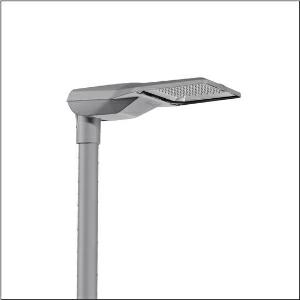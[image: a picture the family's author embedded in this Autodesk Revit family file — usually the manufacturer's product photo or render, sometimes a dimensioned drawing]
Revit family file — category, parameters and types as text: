
# Revit family: streetlight_sl_21_midi___st1_0a_5xe7d63a08nb_cbba
name_source: partatom
category: Lighting Fixtures
units: mm (PartAtom-declared; Revit-internal decimal feet)

## family parameters
Cut with Voids When Loaded = No
Host = Face
Light Source = No
Part Type = Normal
Room Calculation Point = No
Round Connector Dimension = Use Diameter
Shared = No

## types (1)
- --- (1 x LED, 20350 lm, 151.2 W, 2700K)
    Apparent Load = 151 VA
    CIE Flux Codes = 40 73 97 100 100
    Color Rendering = 70
    Color Temperature = 2700K
    Default Elevation = 1800 mm
    Description = Streetlight SL 21 midi, mast luminaire, primary light control with lens, of PMMA, primary optical cover: cover, of toughened safety glass, transparent, light distribution: ST1.0a, light emission: direct distribution, primary light characteristic: asymmetric, installation type: post-top, side-entry, LED, 3G 1.5mm², High Power LED, rated luminous flux: 20.350lm, luminous efficacy: 135lm/W, light colour: 727, colour temperature: 2700K, control: overheat protection, constant luminous flux control, time-dependent luminous flux control, flexible luminous flux parameterisation, mains connection: 220..240V, AC, 50/60Hz, connection cable pre-assembled, cable length: 12,5m, wiring characteristics: H07RN-F, start of lifetime: 151W, end of service life: 157W, reduction: 70W, luminaire housing, of diecast aluminium, powder-coated, Siteco® metallic grey (DB 702S), corrosivity category C5 mid according to DIN EN ISO 12944, please order mast flange separately, inclination adjustable: 0°, 5°, 10°, 15°, sealing non-destructively replaceable, multi-level sealing system, length: 644mm, width: 335mm, height: 110mm, mast flange for spigot size: 42mm (side-entry): 5XC10008XM4, 60/48mm (side-entry/post-top): 5XC10108XM2, 76/60mm (side-entry/post-top): 5XC10108XM1, protection rating (complete): IP66, insulation class (complete): insulation class II (safety insulation), certification: CE, ENEC, ENEC+, VDE, impact resistance: IK09, permissible operating ambient temperature for outdoor applications: -40..+50°C, standard-compliant lighting for roads and squares, packaging unit: 1 piece

Light Distribution: ST1.0a
    Height = 111 mm
    Lamp = 1 x LED
    Lamp Light Flux = 20350 lm
    Lamp Power = 151.2 W
    Lamp count = 1
    Length = 644 mm
    Luminous efficacy = 135 lm/W
    Manufacturer = Siteco
    ModVariant = No
    Model = 5XE7D63A08NB
    Number of Poles = 1
    OnlyDefault = Yes
    Power Factor = 1
    Product Name = Streetlight SL 21 midi | ST1.0a
    Product group = mast luminaire | pylon top
    ProductGroupID = 6100
    Protection Class = Protection class II
    Protection Degree = IP 66
    RLX_Detail_Level = 1
    RLX_Emergency_Light_Flux = 0 lm
    RLX_Emergency_Type = 0
    RLX_Emergency_Type_DB = No
    RlxData = <blob elided: 90445 chars, md5=b1b140c7>
    Socket = socket
    Standby Power = 0 W
    System Light Flux = 20350 lm
    System Power = 151 W
    Type Comments = factory setting: luminous flux: 100 % | Output Level: 100 % | 802 mA
    Type Image = l_1004298.jpg
    URL = http://relux.com
    VarID = @adj_103005
    Voltage = 0 V
    Weight = 0.00 kg
    Width = 336 mm

## geometry (parser evidence)
native form markers: Blend x4, Sweep x12
no freeform markers — native parametric forms only
